# Revit family: NAU_Naughtone_Stng_Rhyme_EndB1
name_source: partatom
category: Furniture
revit_build: Autodesk Revit 2018 (Build: 20170223_1515(x64)
units: mm (PartAtom-declared; Revit-internal decimal feet)

## family parameters
Always vertical = Yes
Cut with Voids When Loaded = No
OmniClass Number = 23.40.20.00
OmniClass Title = General Furniture and Specialties
Room Calculation Point = No
Shared = Yes
Work Plane-Based = No

## types (2) — shared parameters
Assembly Code = E2020200
AssetType = Movable
BIMObjectName = NAU_Naughtone_Seating_Rhyme_EndB
Category = Pr_40_50_12 : Chairs, seats and benches
Color = Various
DurationUnit = year
Finish = Fabric Upholstery
IfcExportAs = IfcFurnishingElementType
IfcExportType = CHAIR
Keynote = Pr_40_50_12
MainColor = Various
ManufacturerAddress = Knaresborough Tech Park, Manse Lane, Knaresborough, HG5 8LF
ManufacturerName = Naughtone
ManufacturerURL = www.naughtone.com
Material = Plinth in Black, White or 14 other RAL finishes
NBSDescription = Seating
NBSReference = 45-35-72/352
Name = Seating_Rhyme_EndB_Naughtone
NominalLength = 1400 mm  [stored 4.59318 ft]
NominalWidth = 1400 mm  [stored 4.59318 ft]
ProductInformation = www.naughtone.com/products/rhyme/
Revision = 0
Shape = Rectangular
SustainabilityPerformance = FSC certified. FISP certified. ISO 14001
URL = www.naughtone.com
Uniclass2015Code = Pr_40_50_12
Uniclass2015Title = Chairs, seats and benches
Version = 1
WarrantyDescription = Request warranty information from naughtone
WarrantyDurationLabor = 7
WarrantyDurationParts = 7
WarrantyDurationUnit = year

## per-type parameters (varying)
| type | Description | IsHighBack | IsLowBack | Model | ModelNumber | ModelReference | NominalHeight | Size |
| Rhyme End B_RYMENDB | Rhyme End B | Yes | No | RYMENDB | RYMENDB | Rhyme End B | 1355 mm  [stored 4.44554 ft] | 1400 x 1400 x 1355mm |
| Rhyme Low End B_RYMLOENDB | Rhyme Low End B | No | Yes | RYMLOENDB | RYMLOENDB | Rhyme Low End B | 850 mm  [stored 2.78871 ft] | 1400 x 1400 x 850mm |

note: [stored X ft] marks values corroborated as IEEE doubles in the binary element streams (Revit-internal decimal feet)

## geometry (parser evidence)
native form markers: Sweep x2
no freeform markers — native parametric forms only
